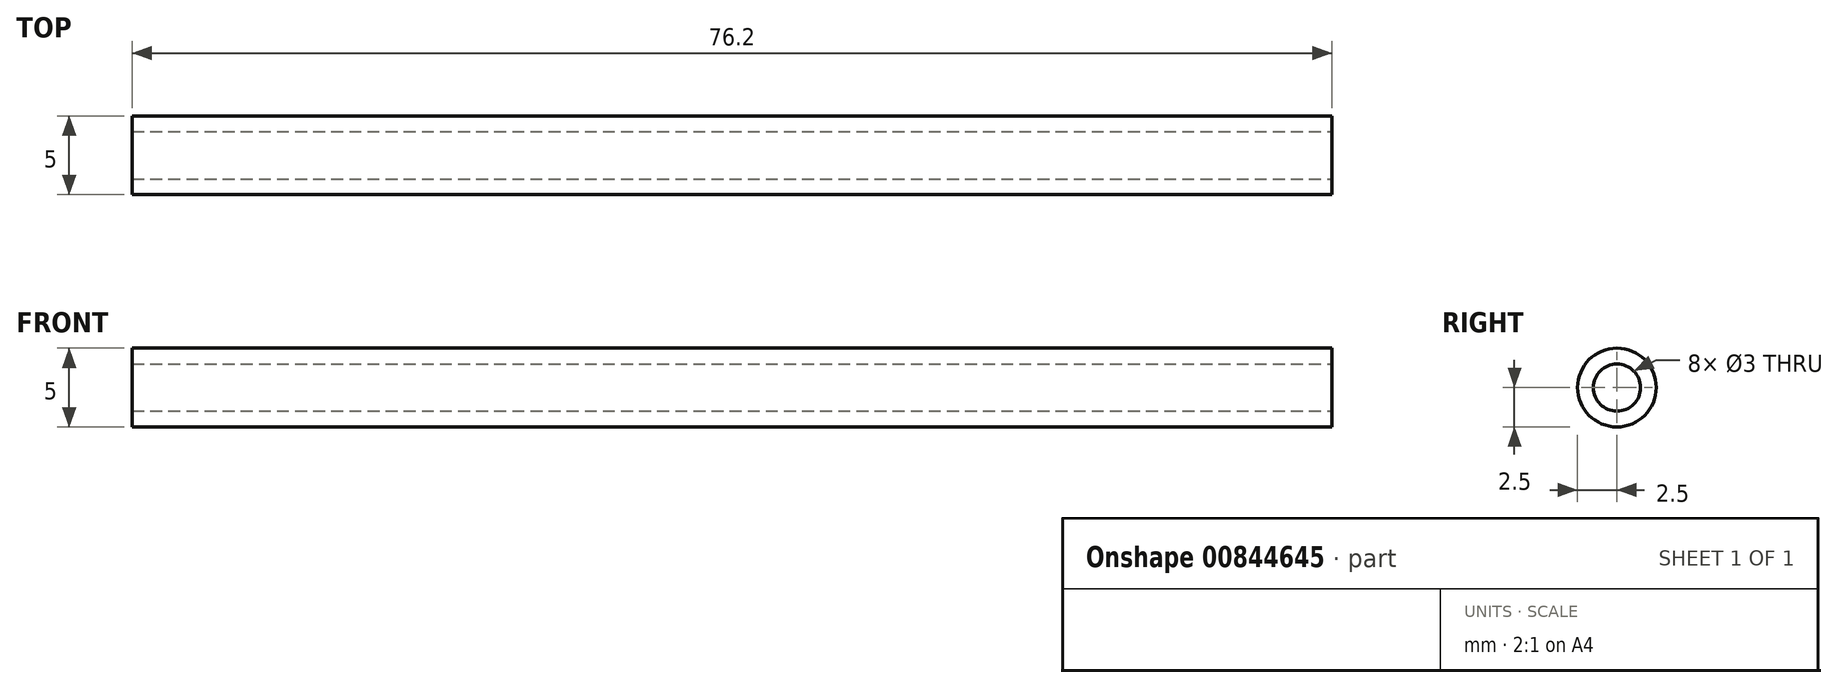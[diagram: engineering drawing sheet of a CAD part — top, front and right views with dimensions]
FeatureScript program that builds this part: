
annotation { "Feature Type Name" : "Feature", "Feature Type Description" : "" }
export const myFeature = defineFeature(function(context is Context, id is Id, definition is map)
    precondition{}
    {
        {
            var Q0;
            Q0=qCreatedBy(makeId("Right.planeOp"),FACE);
            var sketch = newSketch(context, id + "F0", { "sketchPlane" : qUnion([Q0])});
            skCircle(sketch, "E0", {"center": v(0, 0) * mm, "radius": 1.5 * mm});
            skCircle(sketch, "E1", {"center": v(0, 0) * mm, "radius": 2.5 * mm});
            skSolve(sketch);
        }
        {
            var Q0;
            Q0 = qSketchRegion(id + "F0", true);
            extrude(context, id + "F1", {"entities" : qUnion([Q0]), "oppositeDirection" : true, "depth" : 76.2 * mm, "offsetDistance" : 25 * mm, "symmetric" : true});
        }
    });
